# Revit family: QF_NuovAIR_P10.1----
name_source: partatom
category: Specialty Equipment
units: mm (PartAtom-declared; Revit-internal decimal feet)

## family parameters
Always vertical = Yes
Cut with Voids When Loaded = No
Part Type = Normal
Room Calculation Point = No
Round Connector Dimension = Use Diameter
Shared = No
Work Plane-Based = No

## types (6) — shared parameters
Accessory = No
CE Approved = Yes
Conn Plug = only cable
D15 = 15 mm  [stored 0.0492126 ft]
Depth Actual = 853 mm  [stored 2.79856 ft]
Description = Blast Chiller, 8-12 tray GN1/1 - 60x40
Direct Waste Size = 0 mm
DoorH = 920 mm  [stored 3.01837 ft]
Elec Connection Height = 1160 mm  [stored 3.80577 ft]
Electric power = 2900000 W
Foodservice Equipment Identifier = Yes
Height Actual = 1690 mm
Identify Quantity as Lot = No
Item Number = P10.1
Keynote = 0
Legs_R1 = 30 mm  [stored 0.0984252 ft]
Legs_R2 = 25 mm  [stored 0.082021 ft]
Length Actual = 820 mm  [stored 2.69029 ft]
Main switch integrated = No
Manufacturer = NUOVAIR
Mat_Case = QF_Stainless-Brushed
Mat_Clearance = QF_Clearance
Mat_Handle = QF_Stainless-Brushed
Mat_Legs = QF_Stainless-Brushed
Model = P10.1
Number of Poles = 3
Phase = 3
Potential Equalisation = Yes
Refrigerant Compressor Remote = No
Refrigerant Type = R452a
Refrigeration Liquid Line Size = 0 mm
Refrigeration Suction Line Size = 0 mm
URL Cutsheet = P10.1-en.pdf
URL Manufacturer = https://www.nuovair.com
Volt Free Conn = No
Weight = 180.00 kg
zero-valued in all types: Direct Waste Connection Height

## per-type parameters (varying)
| type | Cycle | FL Amps | RH | Volts |
| P10.1_LH_400V 50A | 50 Hz | 6 A | No | 400 V |
| P10.1_RH_400V 50A | 50 Hz | 6 A | Yes | 400 V |
| P10.1_LH_440V 60A | 60 Hz | 7 A | No | 440 V |
| P10.1_RH_440V 60A | 60 Hz | 7 A | Yes | 440 V |
| P10.1_LH_230V 60A | 60 Hz | 13 A | No | 230 V |
| P10.1_RH_230V 60A | 60 Hz | 13 A | Yes | 230 V |

note: [stored X ft] marks values corroborated as IEEE doubles in the binary element streams (Revit-internal decimal feet)

## geometry (parser evidence)
native form markers: Sweep x10
no freeform markers — native parametric forms only
